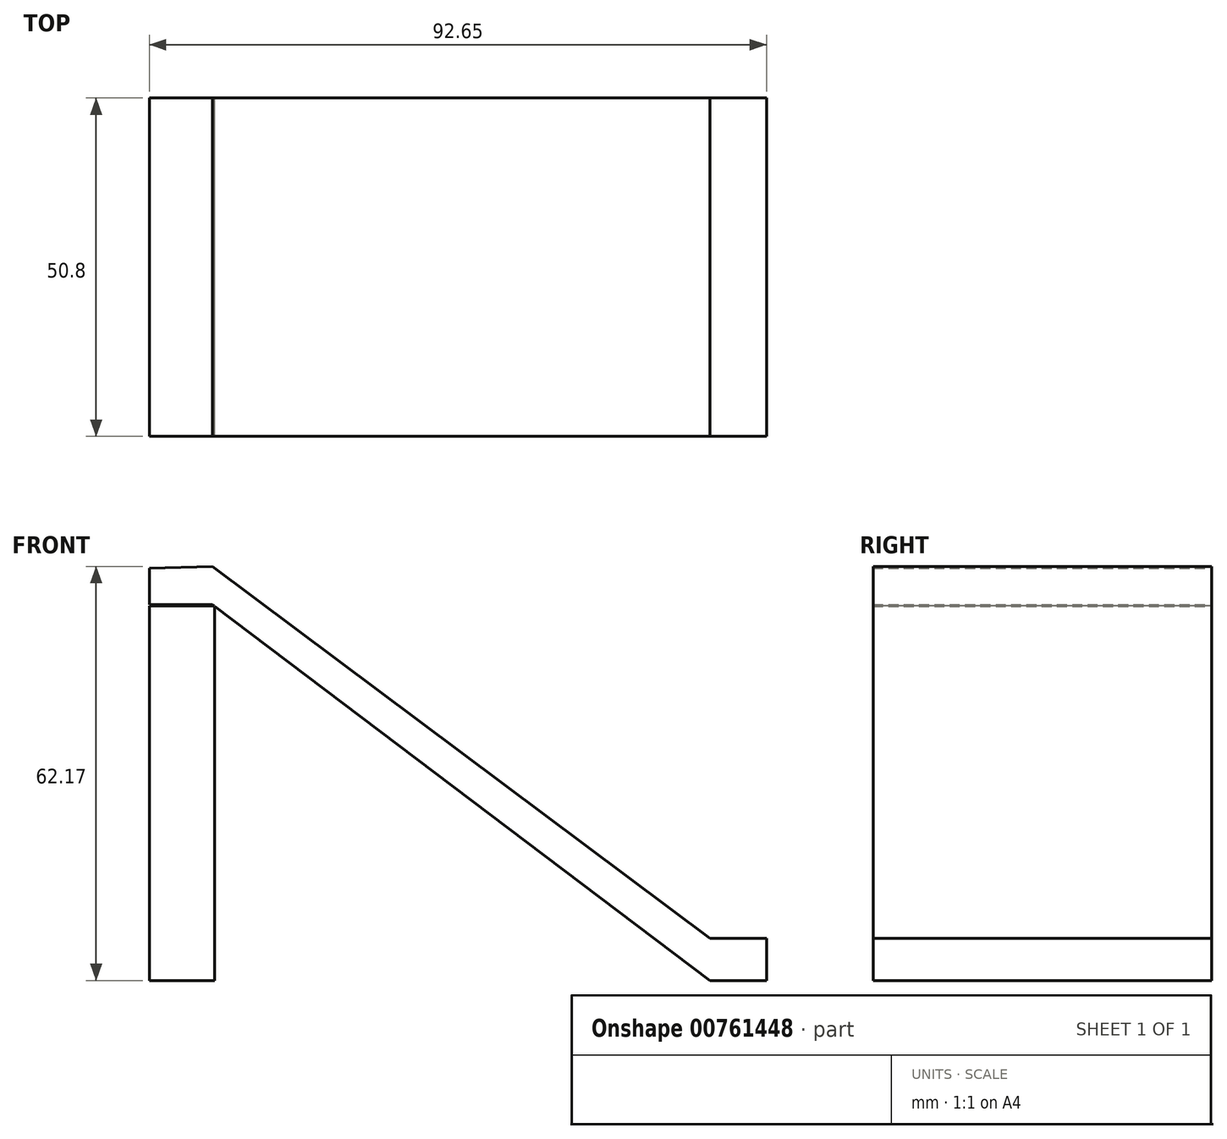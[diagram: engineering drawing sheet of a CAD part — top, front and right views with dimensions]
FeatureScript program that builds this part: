
annotation { "Feature Type Name" : "Feature", "Feature Type Description" : "" }
export const myFeature = defineFeature(function(context is Context, id is Id, definition is map)
    precondition{}
    {
        {
            var Q0;
            Q0=qCreatedBy(makeId("Front.planeOp"),FACE);
            var sketch = newSketch(context, id + "F0", { "sketchPlane" : qUnion([Q0])});
            skLineSegment(sketch, "E0", {"start": v(-57.62, 61.87) * mm, "end": v(-57.62, 56.4) * mm});
            skLineSegment(sketch, "E1", {"start": v(-57.62, 56.4) * mm, "end": v(-48.2, 56.4) * mm});
            skLineSegment(sketch, "E2", {"start": v(-48.2, 56.4) * mm, "end": v(26.5, 0) * mm});
            skLineSegment(sketch, "E3", {"start": v(26.5, 0) * mm, "end": v(35, 0) * mm});
            skLineSegment(sketch, "E4", {"start": v(35, 0) * mm, "end": v(35, 6.3) * mm});
            skLineSegment(sketch, "E5", {"start": v(35, 6.3) * mm, "end": v(26.5, 6.3) * mm});
            skLineSegment(sketch, "E6", {"start": v(26.5, 6.3) * mm, "end": v(-48.2, 62.17) * mm});
            skLineSegment(sketch, "E7", {"start": v(-48.2, 62.17) * mm, "end": v(-57.62, 61.87) * mm});
            skSolve(sketch);
        }
        {
            var Q0;
            Q0 = qSketchRegion(id + "F0", true);
            extrude(context, id + "F1", {"entities" : qUnion([Q0]), "depth" : 50.8 * mm, "offsetDistance" : 25.4 * mm});
        }
        {
            var Q0;
            Q0=qCreatedBy(makeId("Front.planeOp"),FACE);
            var sketch = newSketch(context, id + "F2", { "sketchPlane" : qUnion([Q0])});
            skLineSegment(sketch, "E8", {"start": v(-57.66, 56.21) * mm, "end": v(-47.86, 56.21) * mm});
            skLineSegment(sketch, "E9", {"start": v(-47.86, 56.21) * mm, "end": v(-47.86, 0) * mm});
            skLineSegment(sketch, "E10", {"start": v(-47.86, 0) * mm, "end": v(-57.66, 0) * mm});
            skLineSegment(sketch, "E11", {"start": v(-57.66, 0) * mm, "end": v(-57.66, 56.21) * mm});
            skSolve(sketch);
        }
        {
            var Q0;
            Q0=makeQuery(id+"F2.imprint","IMPRINT",FACE,{"disambiguationData":[TD([[makeQuery(id+"F2.imprint","IMPRINT",EDGE,{"derivedFrom":sQuery(id+"F2.wireOp",EDGE,"E8")}),-1.0]])]});
            extrude(context, id + "F3", {"entities" : qUnion([Q0]), "operationType" : NewBodyOperationType.ADD, "depth" : 50.8 * mm, "offsetDistance" : 25.4 * mm});
        }
    });
